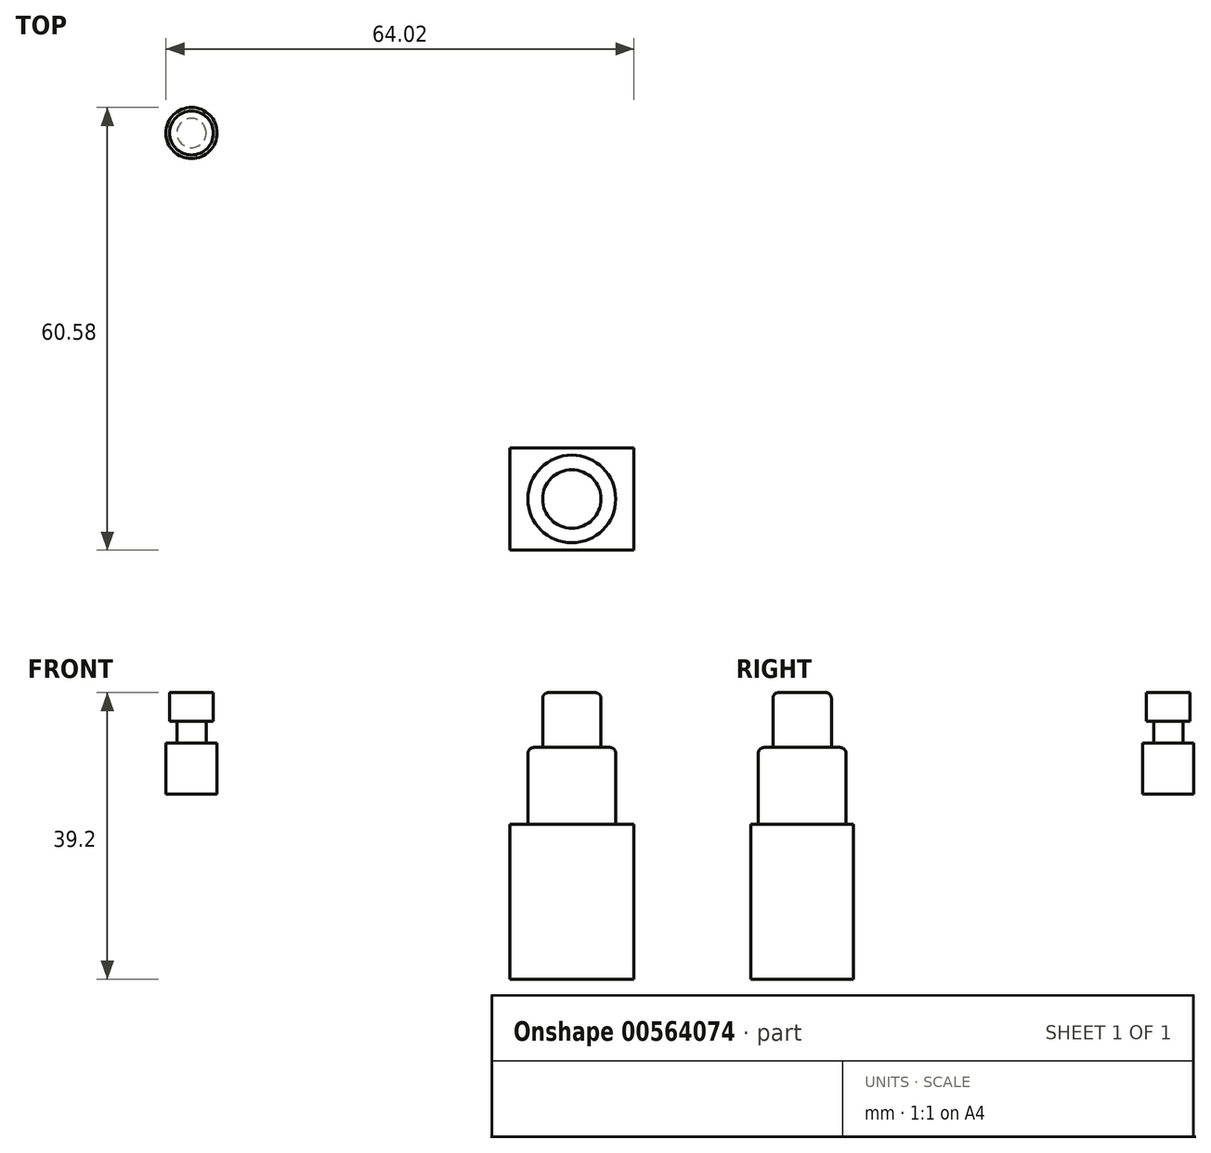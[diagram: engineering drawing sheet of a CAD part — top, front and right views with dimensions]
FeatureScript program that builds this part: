
annotation { "Feature Type Name" : "Feature", "Feature Type Description" : "" }
export const myFeature = defineFeature(function(context is Context, id is Id, definition is map)
    precondition{}
    {
        {
            var Q0;
            Q0=qCreatedBy(makeId("Top.planeOp"),FACE);
            var sketch = newSketch(context, id + "F0", { "sketchPlane" : qUnion([Q0])});
            skCircle(sketch, "E0", {"center": v(-52.02, 0) * mm, "radius": 3 * mm});
            skCircle(sketch, "E1", {"center": v(-52.02, 0) * mm, "radius": 3.5 * mm});
            skCircle(sketch, "E2", {"center": v(-52.02, 0) * mm, "radius": 2 * mm});
            skSolve(sketch);
        }
        {
            var Q0;
            Q0=makeQuery(id+"F0.imprint","IMPRINT",FACE,{"disambiguationData":[TD([[makeQuery(id+"F0.imprint","IMPRINT",EDGE,{"derivedFrom":sQuery(id+"F0.wireOp",EDGE,"E0")}),1.0]])]});
            var Q1;
            Q1=makeQuery(id+"F0.imprint","IMPRINT",FACE,{"disambiguationData":[TD([[makeQuery(id+"F0.imprint","IMPRINT",EDGE,{"derivedFrom":sQuery(id+"F0.wireOp",EDGE,"E2")}),1.0]])]});
            extrude(context, id + "F1", {"entities" : qUnion([Q0, Q1]), "oppositeDirection" : true, "depth" : 3.9 * mm, "offsetDistance" : 25 * mm});
        }
        {
            var Q0;
            Q0=makeQuery(id+"F0.imprint","IMPRINT",FACE,{"disambiguationData":[TD([[makeQuery(id+"F0.imprint","IMPRINT",EDGE,{"derivedFrom":sQuery(id+"F0.wireOp",EDGE,"E2")}),1.0]])]});
            extrude(context, id + "F2", {"entities" : qUnion([Q0]), "operationType" : NewBodyOperationType.ADD, "oppositeDirection" : true, "depth" : 6.9 * mm, "offsetDistance" : 25 * mm});
        }
        {
            var Q0;
            Q0=makeQuery(id+"F0.imprint","IMPRINT",FACE,{"disambiguationData":[TD([[makeQuery(id+"F0.imprint","IMPRINT",EDGE,{"derivedFrom":sQuery(id+"F0.wireOp",EDGE,"E0")}),-1.0]])]});
            var Q1;
            Q1=makeQuery(id+"F0.imprint","IMPRINT",FACE,{"disambiguationData":[TD([[makeQuery(id+"F0.imprint","IMPRINT",EDGE,{"derivedFrom":sQuery(id+"F0.wireOp",EDGE,"E0")}),1.0]])]});
            var Q2;
            Q2=makeQuery(id+"F0.imprint","IMPRINT",FACE,{"disambiguationData":[TD([[makeQuery(id+"F0.imprint","IMPRINT",EDGE,{"derivedFrom":sQuery(id+"F0.wireOp",EDGE,"E2")}),1.0]])]});
            extrude(context, id + "F3", {"entities" : qUnion([Q0, Q1, Q2]), "operationType" : NewBodyOperationType.ADD, "oppositeDirection" : true, "depth" : 13.9 * mm, "offsetDistance" : 25 * mm, "hasSecondDirection" : true, "secondDirectionOppositeDirection" : true, "secondDirectionDepth" : 6.9 * mm});
        }
        {
            var Q0;
            Q0=qCreatedBy(makeId("Top.planeOp"),FACE);
            var sketch = newSketch(context, id + "F4", { "sketchPlane" : qUnion([Q0])});
            skCircle(sketch, "E3", {"center": v(0, -50.08) * mm, "radius": 4 * mm});
            skCircle(sketch, "E4", {"center": v(0, -50.08) * mm, "radius": 6 * mm});
            skLineSegment(sketch, "E5.bottom", {"start": v(8.5, -57.08) * mm, "end": v(-8.5, -57.08) * mm});
            skLineSegment(sketch, "E5.top", {"start": v(8.5, -43.08) * mm, "end": v(-8.5, -43.08) * mm});
            skLineSegment(sketch, "E5.left", {"start": v(8.5, -57.08) * mm, "end": v(8.5, -43.08) * mm});
            skLineSegment(sketch, "E5.right", {"start": v(-8.5, -57.08) * mm, "end": v(-8.5, -43.08) * mm});
            skSolve(sketch);
        }
        {
            var Q0;
            Q0=makeQuery(id+"F4.imprint","IMPRINT",FACE,{"disambiguationData":[TD([[makeQuery(id+"F4.imprint","IMPRINT",EDGE,{"derivedFrom":sQuery(id+"F4.wireOp",EDGE,"E3")}),1.0]])]});
            extrude(context, id + "F5", {"entities" : qUnion([Q0]), "oppositeDirection" : true, "depth" : 7.5 * mm, "offsetDistance" : 25 * mm});
        }
        {
            var Q0;
            Q0=makeQuery(id+"F4.imprint","IMPRINT",FACE,{"disambiguationData":[TD([[makeQuery(id+"F4.imprint","IMPRINT",EDGE,{"derivedFrom":sQuery(id+"F4.wireOp",EDGE,"E3")}),-1.0]])]});
            var Q1;
            Q1=makeQuery(id+"F4.imprint","IMPRINT",FACE,{"disambiguationData":[TD([[makeQuery(id+"F4.imprint","IMPRINT",EDGE,{"derivedFrom":sQuery(id+"F4.wireOp",EDGE,"E3")}),1.0]])]});
            extrude(context, id + "F6", {"entities" : qUnion([Q0, Q1]), "operationType" : NewBodyOperationType.ADD, "oppositeDirection" : true, "depth" : 18 * mm, "offsetDistance" : 25 * mm, "hasSecondDirection" : true, "secondDirectionOppositeDirection" : true, "secondDirectionDepth" : 7.5 * mm});
        }
        {
            var Q0;
            Q0=makeQuery(id+"F4.imprint","IMPRINT",FACE,{"disambiguationData":[TD([[makeQuery(id+"F4.imprint","IMPRINT",EDGE,{"derivedFrom":sQuery(id+"F4.wireOp",EDGE,"E4")}),-1.0]])]});
            var Q1;
            Q1=makeQuery(id+"F4.imprint","IMPRINT",FACE,{"disambiguationData":[TD([[makeQuery(id+"F4.imprint","IMPRINT",EDGE,{"derivedFrom":sQuery(id+"F4.wireOp",EDGE,"E3")}),1.0]])]});
            var Q2;
            Q2=makeQuery(id+"F4.imprint","IMPRINT",FACE,{"disambiguationData":[TD([[makeQuery(id+"F4.imprint","IMPRINT",EDGE,{"derivedFrom":sQuery(id+"F4.wireOp",EDGE,"E3")}),-1.0]])]});
            extrude(context, id + "F7", {"entities" : qUnion([Q0, Q1, Q2]), "operationType" : NewBodyOperationType.ADD, "oppositeDirection" : true, "depth" : 39.2 * mm, "offsetDistance" : 25 * mm, "hasSecondDirection" : true, "secondDirectionOppositeDirection" : true, "secondDirectionDepth" : 18 * mm});
        }
        {
            var Q0;
            Q0=makeQuery(id+"F6.opExtrude","CAP_EDGE",EDGE,{"disambiguationData":[OSD([sQuery(id+"F4.wireOp",EDGE,"E4")])],"isStart":true});
            var Q1;
            Q1=makeQuery(id+"F5.opExtrude","CAP_EDGE",EDGE,{"disambiguationData":[OSD([sQuery(id+"F4.wireOp",EDGE,"E3")])],"isStart":true});
            fillet(context, id + "F8", {"entities" : qUnion([Q0, Q1]), "radius" : .8 * mm, "tangentPropagation" : true, "allowEdgeOverflow" : false});
        }
    });
